# Revit family: QF_ELECTROLUXPROFESSIONAL_391010_E9GCGH4CE0
name_source: partatom
category: Specialty Equipment
revit_build: Autodesk Revit 2018 (Build: 20190510_1515(x64)
units: mm (PartAtom-declared; Revit-internal decimal feet)

## family parameters
Always vertical = Yes
Cut with Voids When Loaded = No
Part Type = Normal
Room Calculation Point = No
Round Connector Dimension = Use Diameter
Shared = No
Work Plane-Based = No

## types (1)
- QF_ELECTROLUXPROFESSIONAL_391010_E9GCGH4CE0
    Apparent Power = 0 VA
    Conn Conduit = Yes
    Description = 900XP 4 GAS BURNERS 6kW ON ELECTRIC OVEN 400V - TEMP 110/285°C
    Direct Waste Size = 0"
    Electrical Remarks = 400 V/3N ph/50/60 Hz
    FL Amps = 0 A
    Gas Connection Height = 0 mm  [stored 0 ft]
    Gas Size = 1"
    HP = 8 HP
    Manufacturer = ELECTROLUX
    Max Overcurrent Protection = 0 A
    Min Ckt Ampacity = 0 A
    Model = 391010
    Phase = 3
    URL = www.electrolux.com
    URL Cutsheet = www.electrolux.com
    Volts = 400 V
    Watts = 0 W
    Weight in Pounds = 115

note: [stored X ft] marks values corroborated as IEEE doubles in the binary element streams (Revit-internal decimal feet)

## geometry (parser evidence)
native form markers: Blend x20, Sweep x5
no freeform markers — native parametric forms only
